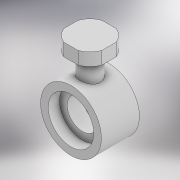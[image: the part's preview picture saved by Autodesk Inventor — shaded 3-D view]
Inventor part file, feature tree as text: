
AUTODESK INVENTOR PART (.ipt)
format: ipt  version: 2022 (Build 260153000, 153)  size: 198,656 bytes
history: native  units: mm
features: sketch x9, extrude x7, projected_geometry x3, revolve x1
ambient origin geometry x8: Origin, YZ Plane, XZ Plane, XY Plane, X Axis, Y Axis, Z Axis, Center Point
bodies: Solid1 (feature_tree)
feature tree (20):
  sketch  "Sketch1"  dims[d0=7.5mm d1=4.0mm d2=8.0mm]
  revolve  "Revolution1"  [1 undecoded]
  extrude  "Extrusion1"  Depth=2.5mm
  extrude  "Extrusion2"  Depth=0.75mm
  extrude  "Extrusion3"  Depth=7.5mm
  extrude  "Extrusion4"  Depth=12.0mm TaperAngle=0.0deg
  extrude  "Extrusion5"  Depth=3.0mm TaperAngle=0.0deg
  extrude  "Extrusion6"  Depth=8.25mm TaperAngle=0.0deg
  extrude  "Extrusion7"  Depth=7.5mm
  sketch  "Sketch2"  dims[d3=2.5mm d4=4.1mm]
  sketch  "Sketch3"  dims[d5=90.0deg d6=0.75mm]
  sketch  "Sketch4"  dims[d7=12.0mm d8=7.5mm]
  projected_geometry  "Projected Loop1"
  sketch  "Sketch6"  dims[d9=12.0mm d10=0.0mm d11=12.0mm d12=0.0mm]
  sketch  "Sketch7"  dims[d13=6.0mm d14=3.0mm d15=0.0mm]
  sketch  "Sketch8"  dims[d16=9.0mm d17=8.25mm d18=0.0mm]
  sketch  "Sketch9"  dims[d19=8.25mm d20=0.0mm d23=7.5mm]
  projected_geometry  "Projected Loop2"
  sketch  "Sketch10"  dims[d24=10.0mm d25=0.0mm d26=10.0mm d27=0.0mm]
  projected_geometry  "Projected Loop3"
note: 1 required parameter value undecoded (feature->parameter linkage not recoverable at this tier; creation-order binding heuristic only, values carry confidence <= 0.55)
